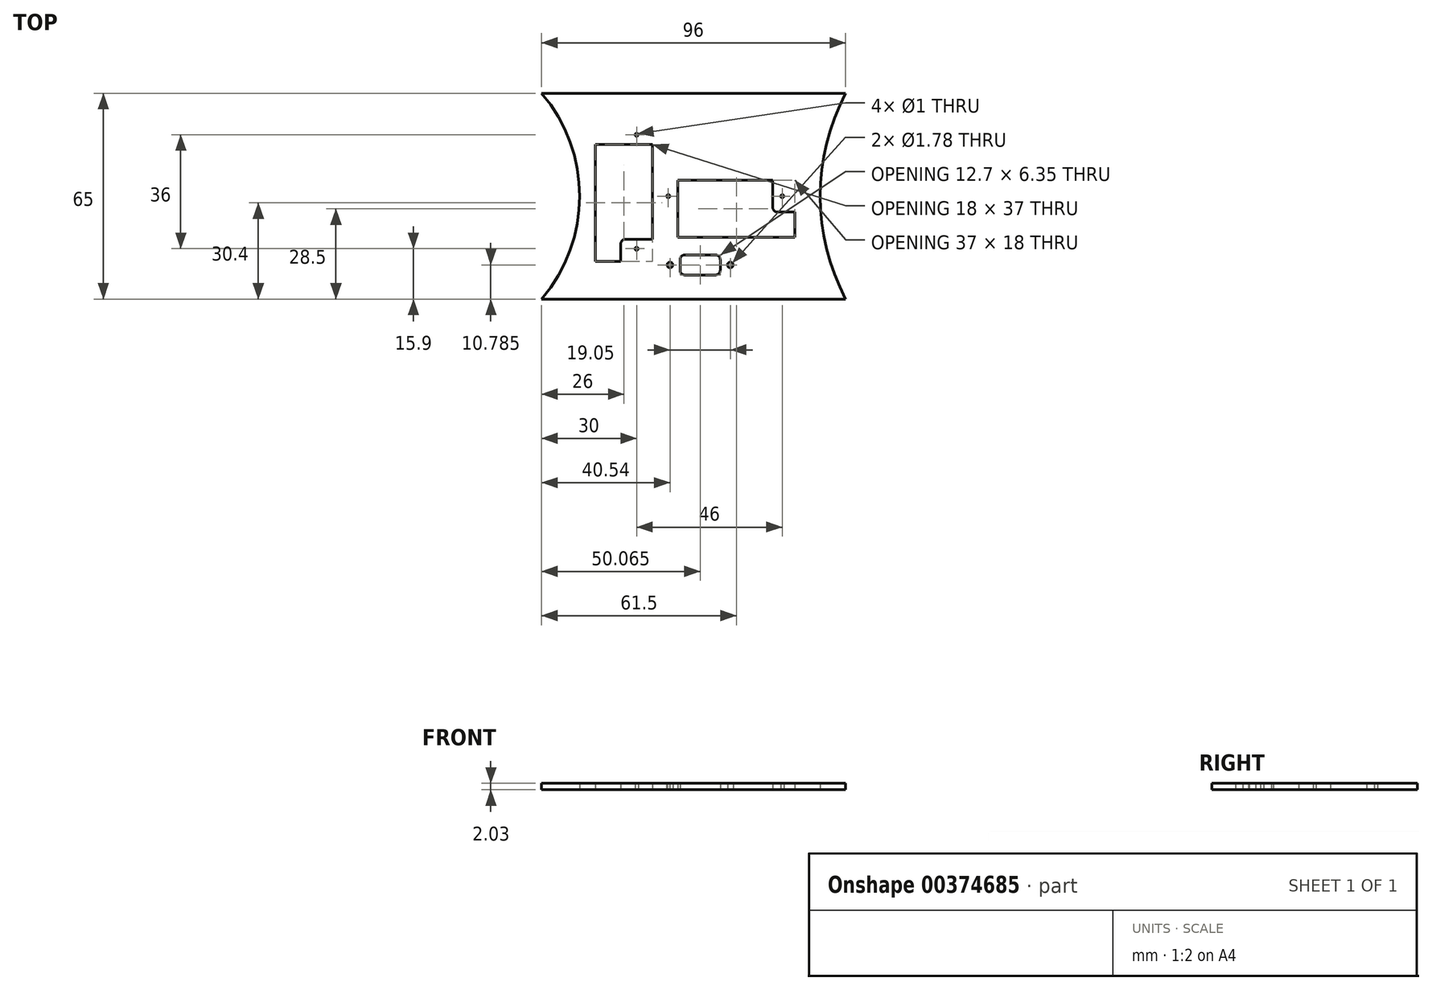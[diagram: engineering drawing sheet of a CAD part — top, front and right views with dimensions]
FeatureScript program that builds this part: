
annotation { "Feature Type Name" : "Feature", "Feature Type Description" : "" }
export const myFeature = defineFeature(function(context is Context, id is Id, definition is map)
    precondition{}
    {
        {
            var Q0;
            Q0=qCreatedBy(makeId("Top.planeOp"),FACE);
            var sketch = newSketch(context, id + "F0", { "sketchPlane" : qUnion([Q0])});
            skCircle(sketch, "E0", {"center": v(19.6, -21.71) * mm, "radius": 0.89 * mm});
            skCircle(sketch, "E1.1.0.0", {"center": v(0.54, -21.71) * mm, "radius": 0.89 * mm});
            skPoint(sketch, "E2.middle", {"position": v(10.07, -21.71) * mm});
            skLineSegment(sketch, "E3.bottom", {"start": v(-2, -16) * mm, "end": v(22.13, -16) * mm, "construction": true});
            skLineSegment(sketch, "E3.top", {"start": v(-2, -27.43) * mm, "end": v(22.13, -27.43) * mm});
            skLineSegment(sketch, "E3.left", {"start": v(-2, -16) * mm, "end": v(-2, -27.43) * mm});
            skLineSegment(sketch, "E3.right", {"start": v(22.13, -16) * mm, "end": v(22.13, -27.43) * mm});
            skLineSegment(sketch, "E4.bottom", {"start": v(14.92, -18.54) * mm, "end": v(5.22, -18.54) * mm});
            skLineSegment(sketch, "E4.top", {"start": v(14.92, -24.89) * mm, "end": v(5.22, -24.89) * mm});
            skLineSegment(sketch, "E4.left", {"start": v(16.42, -20.04) * mm, "end": v(16.42, -23.39) * mm});
            skLineSegment(sketch, "E4.right", {"start": v(3.72, -20.04) * mm, "end": v(3.72, -23.39) * mm});
            skLineSegment(sketch, "E5", {"start": v(10.07, -18.54) * mm, "end": v(10.07, -24.89) * mm, "construction": true});
            skLineSegment(sketch, "E6", {"start": v(0.54, -21.71) * mm, "end": v(19.6, -21.71) * mm, "construction": true});
            skArc(sketch, "E7.filletArc", {"start": v(5.22, -18.54) * mm, "mid": v(4.15, -18.98) * mm, "end": v(3.72, -20.04) * mm});
            skPoint(sketch, "E8.visualSharp", {"position": v(3.72, -24.89) * mm});
            skArc(sketch, "E8.filletArc", {"start": v(3.72, -23.39) * mm, "mid": v(4.15, -24.45) * mm, "end": v(5.22, -24.89) * mm});
            skPoint(sketch, "E9.visualSharp", {"position": v(16.42, -24.89) * mm});
            skArc(sketch, "E9.filletArc", {"start": v(14.92, -24.89) * mm, "mid": v(15.98, -24.45) * mm, "end": v(16.42, -23.39) * mm});
            skPoint(sketch, "E10.visualSharp", {"position": v(16.42, -18.54) * mm});
            skArc(sketch, "E10.filletArc", {"start": v(16.42, -20.04) * mm, "mid": v(15.98, -18.98) * mm, "end": v(14.92, -18.54) * mm});
            skLineSegment(sketch, "E11.top", {"start": v(3, -5) * mm, "end": v(3, 5) * mm});
            skCircle(sketch, "E12", {"center": v(0, 0) * mm, "radius": 0.5 * mm});
            skCircle(sketch, "E13.MirrorC", {"center": v(36, 0) * mm, "radius": 0.5 * mm});
            skCircle(sketch, "E14", {"center": v(26.4, 0) * mm, "radius": 2.5 * mm, "construction": true});
            skLineSegment(sketch, "E15.MirrorCS", {"start": v(18, -13) * mm, "end": v(3, -13) * mm});
            skLineSegment(sketch, "E16.MirrorCS", {"start": v(3, -5) * mm, "end": v(3, -13) * mm});
            skLineSegment(sketch, "E17.MirrorCS", {"start": v(33, 5) * mm, "end": v(33, -3.5) * mm});
            skLineSegment(sketch, "E18.MirrorCS", {"start": v(18, 5) * mm, "end": v(33, 5) * mm});
            skLineSegment(sketch, "E19.MirrorCS", {"start": v(18, 5) * mm, "end": v(3, 5) * mm});
            skLineSegment(sketch, "E20.MirrorCS", {"start": v(18, -13) * mm, "end": v(40, -13) * mm});
            skLineSegment(sketch, "E21.MirrorCS", {"start": v(34.5, -5) * mm, "end": v(40, -5) * mm});
            skLineSegment(sketch, "E22", {"start": v(40, -5) * mm, "end": v(40, -13) * mm});
            skPoint(sketch, "E23.visualSharp", {"position": v(33, -5) * mm});
            skArc(sketch, "E23.filletArc", {"start": v(33, -3.5) * mm, "mid": v(33.44, -4.56) * mm, "end": v(34.5, -5) * mm});
            skLineSegment(sketch, "E24", {"start": v(3, -5) * mm, "end": v(33, -5) * mm, "construction": true});
            skLineSegment(sketch, "E25", {"start": v(-28, 0) * mm, "end": v(48, 0) * mm, "construction": true});
            skLineSegment(sketch, "E26.top", {"start": v(-15, 16.4) * mm, "end": v(-5, 16.4) * mm});
            skCircle(sketch, "E27.MirrorC", {"center": v(-10, -16.6) * mm, "radius": 0.5 * mm});
            skCircle(sketch, "E28", {"center": v(-10, -7) * mm, "radius": 2.5 * mm, "construction": true});
            skLineSegment(sketch, "E29.MirrorCS", {"start": v(-23, 1.4) * mm, "end": v(-23, 16.4) * mm});
            skLineSegment(sketch, "E30.MirrorCS", {"start": v(-15, 16.4) * mm, "end": v(-23, 16.4) * mm});
            skLineSegment(sketch, "E31.MirrorCS", {"start": v(-5, -13.6) * mm, "end": v(-13.5, -13.6) * mm});
            skLineSegment(sketch, "E32.MirrorCS", {"start": v(-5, 1.4) * mm, "end": v(-5, -13.6) * mm});
            skLineSegment(sketch, "E33.MirrorCS", {"start": v(-5, 1.4) * mm, "end": v(-5, 16.4) * mm});
            skLineSegment(sketch, "E34.MirrorCS", {"start": v(-23, 1.4) * mm, "end": v(-23, -20.6) * mm});
            skLineSegment(sketch, "E35.MirrorCS", {"start": v(-15, -15.1) * mm, "end": v(-15, -20.6) * mm});
            skLineSegment(sketch, "E36", {"start": v(-15, -20.6) * mm, "end": v(-23, -20.6) * mm});
            skPoint(sketch, "E37.visualSharp", {"position": v(-15, -13.6) * mm});
            skArc(sketch, "E37.filletArc", {"start": v(-13.5, -13.6) * mm, "mid": v(-14.56, -14.04) * mm, "end": v(-15, -15.1) * mm});
            skLineSegment(sketch, "E38", {"start": v(-15, 16.4) * mm, "end": v(-15, -13.6) * mm, "construction": true});
            skLineSegment(sketch, "E39", {"start": v(-5, 1.4) * mm, "end": v(-23, 1.4) * mm, "construction": true});
            skLineSegment(sketch, "E40", {"start": v(18, 5) * mm, "end": v(18, -13) * mm, "construction": true});
            skCircle(sketch, "E41.MirrorC", {"center": v(-10, 19.4) * mm, "radius": 0.5 * mm});
            skLineSegment(sketch, "E42", {"start": v(48, 32.5) * mm, "end": v(48, -32.5) * mm, "construction": true});
            skLineSegment(sketch, "E43", {"start": v(-28, 32.5) * mm, "end": v(-28, -32.5) * mm, "construction": true});
            skLineSegment(sketch, "E44", {"start": v(-28, 32.5) * mm, "end": v(-40, 32.5) * mm});
            skLineSegment(sketch, "E45", {"start": v(-40, 32.5) * mm, "end": v(56, 32.5) * mm});
            skLineSegment(sketch, "E46.MirrorCS", {"start": v(-40, -32.5) * mm, "end": v(56, -32.5) * mm});
            skArc(sketch, "E47", {"start": v(56, 32.5) * mm, "mid": v(48, 0) * mm, "end": v(56, -32.5) * mm});
            skArc(sketch, "E48", {"start": v(-40, -32.5) * mm, "mid": v(-28, 0) * mm, "end": v(-40, 32.5) * mm});
            skSolve(sketch);
        }
        {
            var Q0;
            Q0=makeQuery(id+"F0.imprint","IMPRINT",FACE,{"disambiguationData":[TD([[makeQuery(id+"F0.imprint","IMPRINT",EDGE,{"derivedFrom":sQuery(id+"F0.wireOp",EDGE,"E0")}),-1.0]])]});
            extrude(context, id + "F1", {"entities" : qUnion([Q0]), "depth" : 2.03 * mm});
        }
    });
